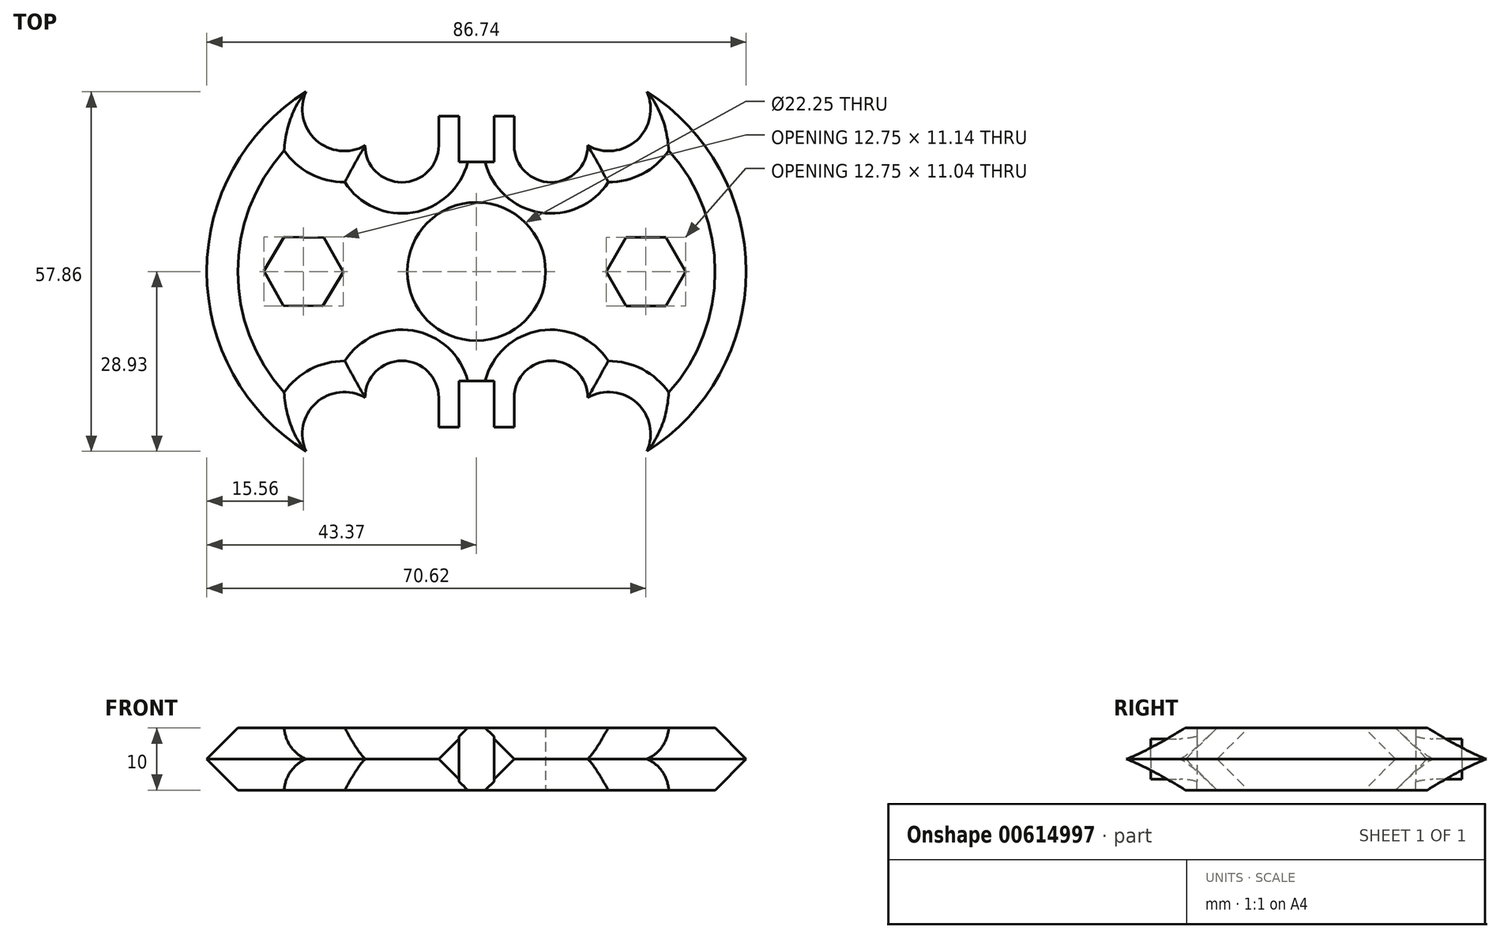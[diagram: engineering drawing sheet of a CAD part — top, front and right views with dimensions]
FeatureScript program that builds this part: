
annotation { "Feature Type Name" : "Feature", "Feature Type Description" : "" }
export const myFeature = defineFeature(function(context is Context, id is Id, definition is map)
    precondition{}
    {
        {
            var Q0;
            Q0=qCreatedBy(makeId("Top.planeOp"),FACE);
            var sketch = newSketch(context, id + "F0", { "sketchPlane" : qUnion([Q0])});
            skCircle(sketch, "E0.cCircle", {"center": v(27.25, 0) * mm, "radius": 5.52 * mm, "construction": true});
            skLineSegment(sketch, "E0.0", {"start": v(24.06, 5.52) * mm, "end": v(30.44, 5.52) * mm});
            skLineSegment(sketch, "E0.1", {"start": v(30.44, 5.52) * mm, "end": v(33.62, 0) * mm});
            skLineSegment(sketch, "E0.2", {"start": v(33.62, 0) * mm, "end": v(30.44, -5.52) * mm});
            skLineSegment(sketch, "E0.3", {"start": v(30.44, -5.52) * mm, "end": v(24.06, -5.52) * mm});
            skLineSegment(sketch, "E0.4", {"start": v(24.06, -5.52) * mm, "end": v(20.87, 0) * mm});
            skLineSegment(sketch, "E0.5", {"start": v(20.87, 0) * mm, "end": v(24.06, 5.52) * mm});
            skPoint(sketch, "E0.0.midPoint", {"position": v(27.25, 5.52) * mm});
            skCircle(sketch, "E1.cCircle", {"center": v(-27.8, 0) * mm, "radius": 5.52 * mm, "construction": true});
            skLineSegment(sketch, "E1.0", {"start": v(-24.54, 5.47) * mm, "end": v(-21.44, -0.1) * mm});
            skLineSegment(sketch, "E1.1", {"start": v(-21.44, -0.1) * mm, "end": v(-24.7, -5.57) * mm});
            skLineSegment(sketch, "E1.2", {"start": v(-24.7, -5.57) * mm, "end": v(-31.08, -5.47) * mm});
            skLineSegment(sketch, "E1.3", {"start": v(-31.08, -5.47) * mm, "end": v(-34.18, 0.1) * mm});
            skLineSegment(sketch, "E1.4", {"start": v(-34.18, 0.1) * mm, "end": v(-30.91, 5.57) * mm});
            skLineSegment(sketch, "E1.5", {"start": v(-30.91, 5.57) * mm, "end": v(-24.54, 5.47) * mm});
            skPoint(sketch, "E1.0.midPoint", {"position": v(-22.99, 2.69) * mm});
            skLineSegment(sketch, "E2", {"start": v(0, -17.62) * mm, "end": v(2.81, -17.62) * mm});
            skLineSegment(sketch, "E3", {"start": v(2.81, -17.62) * mm, "end": v(2.81, -25.02) * mm});
            skLineSegment(sketch, "E4", {"start": v(2.81, -25.02) * mm, "end": v(6.07, -25.02) * mm});
            skLineSegment(sketch, "E5.MirrorCS", {"start": v(2.81, 17.62) * mm, "end": v(2.81, 25.02) * mm});
            skLineSegment(sketch, "E6", {"start": v(2.81, 25.02) * mm, "end": v(6.07, 25.02) * mm});
            skLineSegment(sketch, "E7", {"start": v(2.81, 17.62) * mm, "end": v(0, 17.62) * mm});
            skLineSegment(sketch, "E8.MirrorCS", {"start": v(-2.81, 17.62) * mm, "end": v(-2.81, 25.02) * mm});
            skLineSegment(sketch, "E9.MirrorCS", {"start": v(-2.81, -17.62) * mm, "end": v(-2.81, -25.02) * mm});
            skLineSegment(sketch, "E10", {"start": v(-6.07, 25.02) * mm, "end": v(-2.81, 25.02) * mm});
            skLineSegment(sketch, "E11", {"start": v(-2.81, 17.62) * mm, "end": v(0, 17.62) * mm});
            skLineSegment(sketch, "E12", {"start": v(-2.81, -25.02) * mm, "end": v(-6.07, -25.02) * mm});
            skLineSegment(sketch, "E13", {"start": v(-2.81, -17.62) * mm, "end": v(0, -17.62) * mm});
            skLineSegment(sketch, "E14", {"start": v(6.07, 25.02) * mm, "end": v(6.07, 20.28) * mm});
            skLineSegment(sketch, "E15.MirrorCS", {"start": v(-6.07, 25.02) * mm, "end": v(-6.07, 20.28) * mm});
            skLineSegment(sketch, "E16.MirrorCS", {"start": v(-6.07, -25.02) * mm, "end": v(-6.07, -20.28) * mm});
            skLineSegment(sketch, "E17.MirrorCS", {"start": v(6.07, -25.02) * mm, "end": v(6.07, -20.28) * mm});
            skArc(sketch, "E18", {"start": v(-27.4, 28.93) * mm, "mid": v(-43.37, 0) * mm, "end": v(-27.4, -28.93) * mm});
            skArc(sketch, "E19.MirrorCS", {"start": v(27.4, 28.93) * mm, "mid": v(43.37, 0) * mm, "end": v(27.4, -28.93) * mm});
            skCircle(sketch, "E20", {"center": v(0, 0) * mm, "radius": 11.12 * mm});
            skArc(sketch, "E21", {"start": v(-17.91, 20.28) * mm, "mid": v(-12, 14.36) * mm, "end": v(-6.07, 20.28) * mm});
            skArc(sketch, "E22", {"start": v(-27.4, 28.93) * mm, "mid": v(-25.8, 21.15) * mm, "end": v(-17.91, 20.28) * mm});
            skArc(sketch, "E23.MirrorCS", {"start": v(17.91, 20.28) * mm, "mid": v(12, 14.36) * mm, "end": v(6.07, 20.28) * mm});
            skArc(sketch, "E24.MirrorCS", {"start": v(27.4, 28.93) * mm, "mid": v(25.8, 21.15) * mm, "end": v(17.91, 20.28) * mm});
            skArc(sketch, "E25.MirrorCS", {"start": v(-27.4, -28.93) * mm, "mid": v(-25.8, -21.15) * mm, "end": v(-17.91, -20.28) * mm});
            skArc(sketch, "E26.MirrorCS", {"start": v(-17.91, -20.28) * mm, "mid": v(-12, -14.36) * mm, "end": v(-6.07, -20.28) * mm});
            skArc(sketch, "E27.MirrorCS", {"start": v(17.91, -20.28) * mm, "mid": v(12, -14.36) * mm, "end": v(6.07, -20.28) * mm});
            skArc(sketch, "E28.MirrorCS", {"start": v(27.4, -28.93) * mm, "mid": v(25.8, -21.15) * mm, "end": v(17.91, -20.28) * mm});
            skSolve(sketch);
        }
        {
            var Q0;
            Q0=makeQuery(id+"F0.imprint","IMPRINT",FACE,{"disambiguationData":[TD([[makeQuery(id+"F0.imprint","IMPRINT",EDGE,{"derivedFrom":sQuery(id+"F0.wireOp",EDGE,"E0.0")}),1.0]])]});
            extrude(context, id + "F1", {"entities" : qUnion([Q0]), "depth" : 10 * mm, "offsetDistance" : 25 * mm});
        }
        {
            var Q0;
            Q0=makeQuery(id+"F1.opExtrude","CAP_EDGE",EDGE,{"disambiguationData":[OSD([sQuery(id+"F0.wireOp",EDGE,"E22")])],"isStart":false});
            var Q1;
            Q1=makeQuery(id+"F1.opExtrude","CAP_EDGE",EDGE,{"disambiguationData":[OSD([sQuery(id+"F0.wireOp",EDGE,"E21")])],"isStart":false});
            var Q2;
            Q2=makeQuery(id+"F1.opExtrude","CAP_EDGE",EDGE,{"disambiguationData":[OSD([sQuery(id+"F0.wireOp",EDGE,"E18")])],"isStart":false});
            var Q3;
            Q3=makeQuery(id+"F1.opExtrude","CAP_EDGE",EDGE,{"disambiguationData":[OSD([sQuery(id+"F0.wireOp",EDGE,"E25.MirrorCS")])],"isStart":false});
            var Q4;
            Q4=makeQuery(id+"F1.opExtrude","CAP_EDGE",EDGE,{"disambiguationData":[OSD([sQuery(id+"F0.wireOp",EDGE,"E26.MirrorCS")])],"isStart":false});
            var Q5;
            Q5=makeQuery(id+"F1.opExtrude","CAP_EDGE",EDGE,{"disambiguationData":[OSD([sQuery(id+"F0.wireOp",EDGE,"E27.MirrorCS")])],"isStart":false});
            var Q6;
            Q6=makeQuery(id+"F1.opExtrude","CAP_EDGE",EDGE,{"disambiguationData":[OSD([sQuery(id+"F0.wireOp",EDGE,"E28.MirrorCS")])],"isStart":false});
            var Q7;
            Q7=makeQuery(id+"F1.opExtrude","CAP_EDGE",EDGE,{"disambiguationData":[OSD([sQuery(id+"F0.wireOp",EDGE,"E19.MirrorCS")])],"isStart":false});
            var Q8;
            Q8=makeQuery(id+"F1.opExtrude","CAP_EDGE",EDGE,{"disambiguationData":[OSD([sQuery(id+"F0.wireOp",EDGE,"E24.MirrorCS")])],"isStart":false});
            var Q9;
            Q9=makeQuery(id+"F1.opExtrude","CAP_EDGE",EDGE,{"disambiguationData":[OSD([sQuery(id+"F0.wireOp",EDGE,"E23.MirrorCS")])],"isStart":false});
            var Q10;
            Q10=makeQuery(id+"F1.opExtrude","CAP_EDGE",EDGE,{"disambiguationData":[OSD([sQuery(id+"F0.wireOp",EDGE,"E24.MirrorCS")])],"isStart":true});
            var Q11;
            Q11=makeQuery(id+"F1.opExtrude","CAP_EDGE",EDGE,{"disambiguationData":[OSD([sQuery(id+"F0.wireOp",EDGE,"E19.MirrorCS")])],"isStart":true});
            var Q12;
            Q12=makeQuery(id+"F1.opExtrude","CAP_EDGE",EDGE,{"disambiguationData":[OSD([sQuery(id+"F0.wireOp",EDGE,"E28.MirrorCS")])],"isStart":true});
            var Q13;
            Q13=makeQuery(id+"F1.opExtrude","CAP_EDGE",EDGE,{"disambiguationData":[OSD([sQuery(id+"F0.wireOp",EDGE,"E27.MirrorCS")])],"isStart":true});
            var Q14;
            Q14=makeQuery(id+"F1.opExtrude","CAP_EDGE",EDGE,{"disambiguationData":[OSD([sQuery(id+"F0.wireOp",EDGE,"E26.MirrorCS")])],"isStart":true});
            var Q15;
            Q15=makeQuery(id+"F1.opExtrude","CAP_EDGE",EDGE,{"disambiguationData":[OSD([sQuery(id+"F0.wireOp",EDGE,"E23.MirrorCS")])],"isStart":true});
            var Q16;
            Q16=makeQuery(id+"F1.opExtrude","CAP_EDGE",EDGE,{"disambiguationData":[OSD([sQuery(id+"F0.wireOp",EDGE,"E21")])],"isStart":true});
            var Q17;
            Q17=makeQuery(id+"F1.opExtrude","CAP_EDGE",EDGE,{"disambiguationData":[OSD([sQuery(id+"F0.wireOp",EDGE,"E22")])],"isStart":true});
            var Q18;
            Q18=makeQuery(id+"F1.opExtrude","CAP_EDGE",EDGE,{"disambiguationData":[OSD([sQuery(id+"F0.wireOp",EDGE,"E18")])],"isStart":true});
            var Q19;
            Q19=makeQuery(id+"F1.opExtrude","CAP_EDGE",EDGE,{"disambiguationData":[OSD([sQuery(id+"F0.wireOp",EDGE,"E25.MirrorCS")])],"isStart":true});
            chamfer(context, id + "F2", {"entities" : qUnion([Q0, Q1, Q2, Q3, Q4, Q5, Q6, Q7, Q8, Q9, Q10, Q11, Q12, Q13, Q14, Q15, Q16, Q17, Q18, Q19]), "width" : 5 * mm, "tangentPropagation" : true});
        }
    });
